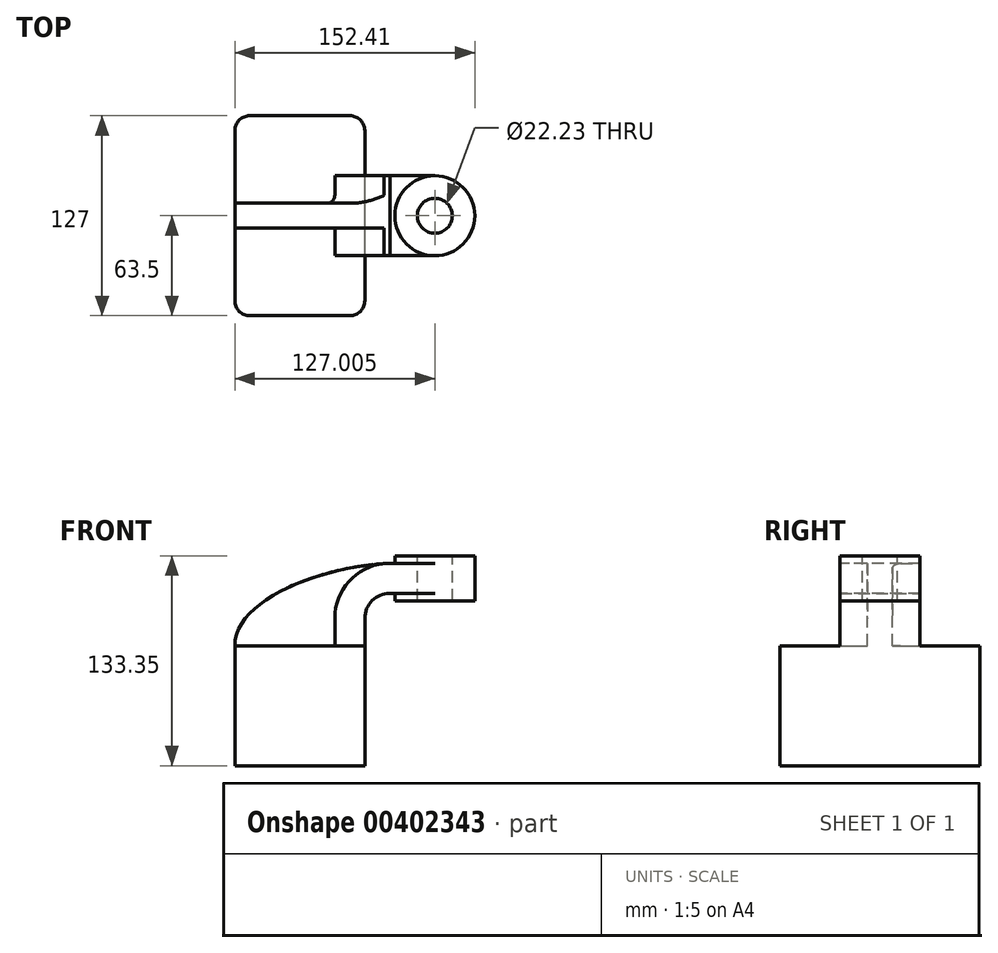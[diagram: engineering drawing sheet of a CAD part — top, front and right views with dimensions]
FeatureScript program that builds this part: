
annotation { "Feature Type Name" : "Feature", "Feature Type Description" : "" }
export const myFeature = defineFeature(function(context is Context, id is Id, definition is map)
    precondition{}
    {
        {
            var Q0;
            Q0=qCreatedBy(makeId("Front.planeOp"),FACE);
            var sketch = newSketch(context, id + "F0", { "sketchPlane" : qUnion([Q0])});
            skLineSegment(sketch, "E0.bottom", {"start": v(41.28, -9.53) * mm, "end": v(-41.28, -9.53) * mm});
            skLineSegment(sketch, "E0.top", {"start": v(41.27, 9.53) * mm, "end": v(-41.28, 9.52) * mm});
            skLineSegment(sketch, "E0.left", {"start": v(41.28, -9.53) * mm, "end": v(41.28, 9.53) * mm});
            skLineSegment(sketch, "E0.right", {"start": v(-41.27, -9.53) * mm, "end": v(-41.28, 9.52) * mm});
            skPoint(sketch, "E0.middle", {"position": v(0, 0) * mm});
            skLineSegment(sketch, "E1.bottom", {"start": v(111.13, 38.1) * mm, "end": v(60.33, 38.1) * mm});
            skLineSegment(sketch, "E1.top", {"start": v(111.13, 66.68) * mm, "end": v(60.33, 66.68) * mm});
            skLineSegment(sketch, "E1.left", {"start": v(111.13, 38.1) * mm, "end": v(111.13, 66.68) * mm});
            skLineSegment(sketch, "E1.right", {"start": v(60.33, 38.1) * mm, "end": v(60.33, 66.68) * mm});
            skPoint(sketch, "E1.middle", {"position": v(85.73, 52.39) * mm});
            skLineSegment(sketch, "E2", {"start": v(41.27, 9.53) * mm, "end": v(41.27, 27) * mm});
            skLineSegment(sketch, "E3", {"start": v(57.15, 42.88) * mm, "end": v(85.73, 42.88) * mm});
            skPoint(sketch, "E4.visualSharp", {"position": v(41.27, 42.88) * mm});
            skArc(sketch, "E4.filletArc", {"start": v(57.15, 42.88) * mm, "mid": v(45.92, 38.23) * mm, "end": v(41.27, 27) * mm});
            skLineSegment(sketch, "E5.0", {"start": v(57.15, 61.93) * mm, "end": v(85.73, 61.93) * mm});
            skArc(sketch, "E5.1", {"start": v(57.15, 61.93) * mm, "mid": v(32.45, 51.7) * mm, "end": v(22.23, 27) * mm});
            skLineSegment(sketch, "E5.2", {"start": v(22.22, 9.53) * mm, "end": v(22.22, 27) * mm});
            skLineSegment(sketch, "E6", {"start": v(85.73, 66.68) * mm, "end": v(85.73, 38.1) * mm});
            skFitSpline(sketch, "E7", {"points": [v(-41.28, 9.52) * mm, v(57.15, 61.93) * mm], "startDerivative": vector(0, 87.13) * mm, "endDerivative": vector(133.17, 5.64) * mm});
            skSolve(sketch);
        }
        {
            var Q0;
            Q0=makeQuery(id+"F0.imprint","IMPRINT",FACE,{"disambiguationData":[TD([[makeQuery(id+"F0.imprint","IMPRINT",EDGE,{"derivedFrom":sQuery(id+"F0.wireOp",EDGE,"E0.bottom")}),-1.0]])]});
            extrude(context, id + "F1", {"entities" : qUnion([Q0]), "endBound" : BoundingType.SYMMETRIC, "depth" : 127 * mm});
        }
        {
            var Q0;
            {var subQ3=sQuery(id+"F0.wireOp",EDGE,"E5.2");Q0=makeQuery(id+"F0.imprint","IMPRINT",FACE,{"disambiguationData":[TD([[makeQuery(id+"F0.imprint","IMPRINT",EDGE,{"derivedFrom":subQ3}),1.0]])]});}
            extrude(context, id + "F2", {"entities" : qUnion([Q0]), "operationType" : NewBodyOperationType.ADD, "endBound" : BoundingType.SYMMETRIC, "depth" : 15.88 * mm});
        }
        {
            var Q0;
            {var subQ4=sQuery(id+"F0.wireOp",EDGE,"E2");Q0=makeQuery(id+"F0.imprint","IMPRINT",FACE,{"disambiguationData":[TD([[makeQuery(id+"F0.imprint","IMPRINT",EDGE,{"derivedFrom":subQ4}),1.0]])]});}
            var Q1;
            {var subQ0=sQuery(id+"F0.wireOp",EDGE,"E3");var subQ1=sQuery(id+"F0.wireOp",EDGE,"E1.right");var subQ2=makeQuery(id+"F0.imprint","INTERSECT",VERTEX,{"derivedFrom":[subQ1,subQ0]});Q1=makeQuery(id+"F0.imprint","IMPRINT",FACE,{"disambiguationData":[TD([[makeQuery(id+"F0.imprint","IMPRINT",EDGE,{"disambiguationData":[TD([[subQ2,-1.0]])],"derivedFrom":subQ1}),-1.0]])]});}
            extrude(context, id + "F3", {"entities" : qUnion([Q0, Q1]), "operationType" : NewBodyOperationType.ADD, "endBound" : BoundingType.SYMMETRIC, "depth" : 50.8 * mm});
        }
        {
            var Q0;
            {var subQ0=sQuery(id+"F0.wireOp",EDGE,"E1.left");Q0=makeQuery(id+"F0.imprint","IMPRINT",FACE,{"disambiguationData":[TD([[makeQuery(id+"F0.imprint","IMPRINT",EDGE,{"derivedFrom":subQ0}),1.0]])]});}
            var Q1;
            Q1=sQuery(id+"F0.wireOp",EDGE,"E6");
            revolve(context, id + "F4", {"operationType" : NewBodyOperationType.ADD, "entities" : qUnion([Q0]), "axis" : qUnion([Q1]), "revolveType" : RevolveType.FULL});
        }
        {
            var Q0;
            Q0=makeQuery(id+"F1.opExtrude","CAP_EDGE",EDGE,{"disambiguationData":[OSD([sQuery(id+"F0.wireOp",EDGE,"E0.left")])],"isStart":false});
            var Q1;
            Q1=makeQuery(id+"F1.opExtrude","CAP_EDGE",EDGE,{"disambiguationData":[OSD([sQuery(id+"F0.wireOp",EDGE,"E0.right")])],"isStart":false});
            var Q2;
            Q2=makeQuery(id+"F1.opExtrude","CAP_EDGE",EDGE,{"disambiguationData":[OSD([sQuery(id+"F0.wireOp",EDGE,"E0.left")])],"isStart":true});
            var Q3;
            Q3=makeQuery(id+"F1.opExtrude","CAP_EDGE",EDGE,{"disambiguationData":[OSD([sQuery(id+"F0.wireOp",EDGE,"E0.right")])],"isStart":true});
            fillet(context, id + "F5", {"entities" : qUnion([Q0, Q1, Q2, Q3]), "radius" : 9.52 * mm, "tangentPropagation" : true, "allowEdgeOverflow" : false});
        }
        {
            var Q0;
            Q0=makeQuery(id+"F2.opExtrude","CAP_EDGE",EDGE,{"disambiguationData":[OSD([sQuery(id+"F0.wireOp",EDGE,"E0.top")])],"isStart":false});
            var Q1;
            Q1=makeQuery(id+"F2.opExtrude","CAP_EDGE",EDGE,{"disambiguationData":[OSD([sQuery(id+"F0.wireOp",EDGE,"E5.1")])],"isStart":false});
            var Q2;
            Q2=makeQuery(id+"F2.opExtrude","CAP_EDGE",EDGE,{"disambiguationData":[OSD([sQuery(id+"F0.wireOp",EDGE,"E5.1")])],"isStart":true});
            var Q3;
            Q3=makeQuery(id+"F2.opExtrude","CAP_EDGE",EDGE,{"disambiguationData":[OSD([sQuery(id+"F0.wireOp",EDGE,"E0.top")])],"isStart":true});
            var Q4;
            Q4=makeQuery(id+"F2.opExtrude","CAP_EDGE",EDGE,{"disambiguationData":[OSD([sQuery(id+"F0.wireOp",EDGE,"E5.2")])],"isStart":true});
            var Q5;
            Q5=makeQuery(id+"F2.opExtrude","CAP_EDGE",EDGE,{"disambiguationData":[OSD([sQuery(id+"F0.wireOp",EDGE,"E5.2")])],"isStart":false});
            fillet(context, id + "F6", {"entities" : qUnion([Q0, Q1, Q2, Q3, Q4, Q5]), "radius" : 5.08 * mm, "tangentPropagation" : true, "allowEdgeOverflow" : false});
        }
        {
            var Q0;
            Q0=makeQuery(id+"F4.opRevolve","SWEPT_FACE",FACE,{"disambiguationData":[OSD([sQuery(id+"F0.wireOp",EDGE,"E1.top")])]});
            var sketch = newSketch(context, id + "F7", { "sketchPlane" : qUnion([Q0])});
            skCircle(sketch, "E8", {"center": v(85.73, 0) * mm, "radius": 11.11 * mm});
            skSolve(sketch);
        }
        {
            var Q0;
            Q0=makeQuery(id+"F7.imprint","IMPRINT",FACE,{"disambiguationData":[TD([[makeQuery(id+"F7.imprint","IMPRINT",EDGE,{"derivedFrom":sQuery(id+"F7.wireOp",EDGE,"E8")}),1.0]])]});
            extrude(context, id + "F8", {"entities" : qUnion([Q0]), "operationType" : NewBodyOperationType.REMOVE, "oppositeDirection" : true, "depth" : 50.55 * mm});
        }
        {
            var Q0;
            Q0=makeQuery(id+"F1.opExtrude","SWEPT_FACE",FACE,{"disambiguationData":[OSD([sQuery(id+"F0.wireOp",EDGE,"E0.bottom")])]});
            extrude(context, id + "F9", {"entities" : qUnion([Q0]), "operationType" : NewBodyOperationType.ADD, "depth" : 57.15 * mm});
        }
    });
